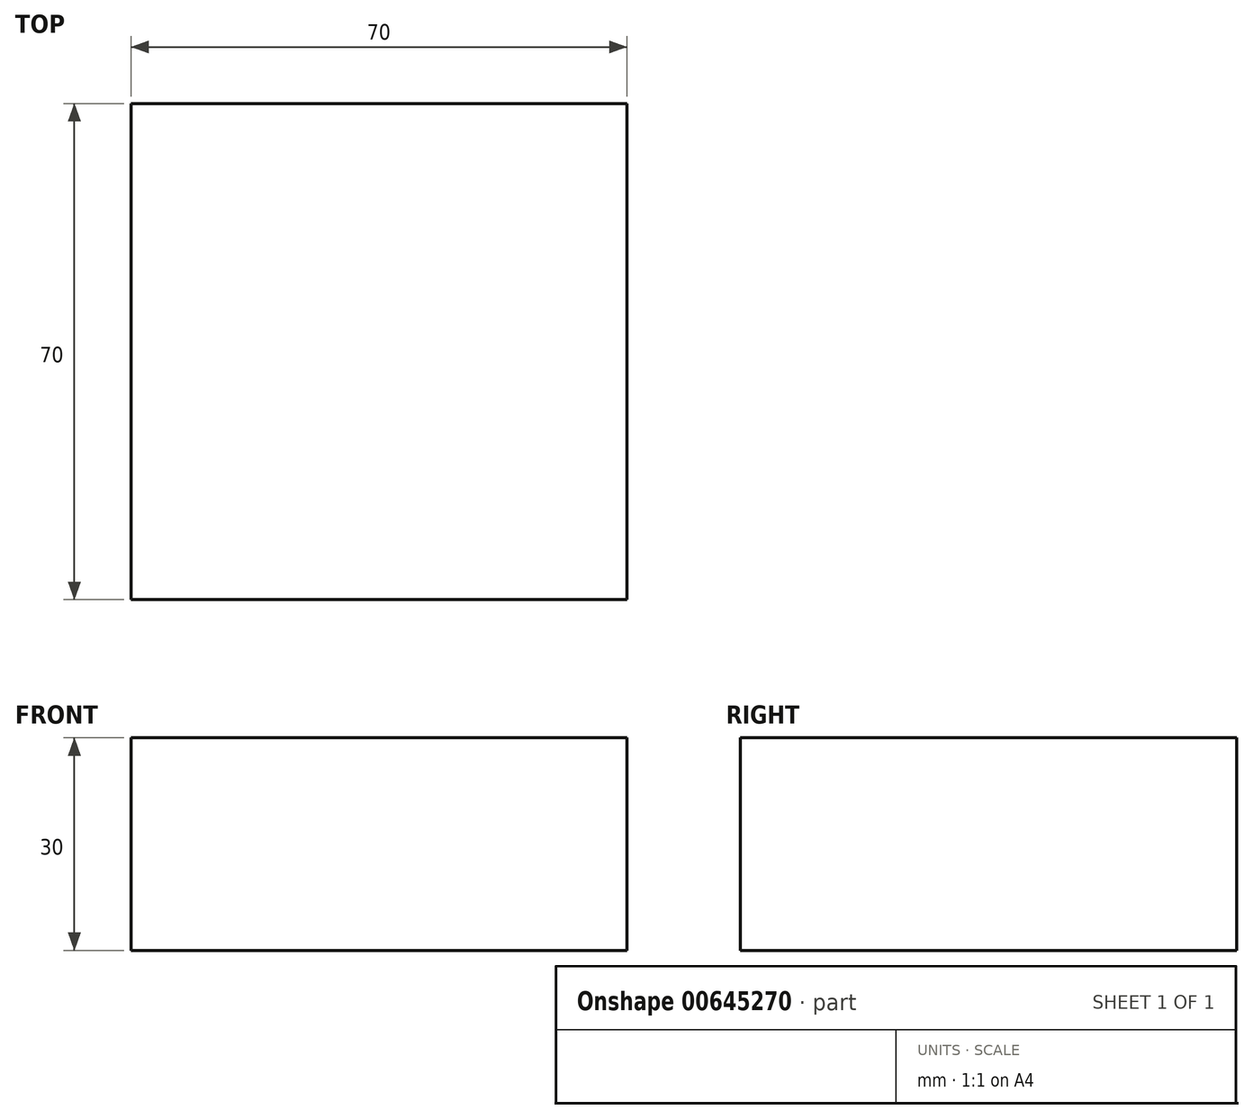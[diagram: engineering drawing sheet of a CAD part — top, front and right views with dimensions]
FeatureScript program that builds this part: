
annotation { "Feature Type Name" : "Feature", "Feature Type Description" : "" }
export const myFeature = defineFeature(function(context is Context, id is Id, definition is map)
    precondition{}
    {
        {
            var Q0;
            Q0=qCreatedBy(makeId("Top.planeOp"),FACE);
            var sketch = newSketch(context, id + "F0", { "sketchPlane" : qUnion([Q0])});
            skLineSegment(sketch, "E0.bottom", {"start": v(-37.1, 44.21) * mm, "end": v(32.9, 44.21) * mm});
            skLineSegment(sketch, "E0.top", {"start": v(-37.1, -25.79) * mm, "end": v(32.9, -25.79) * mm});
            skLineSegment(sketch, "E0.left", {"start": v(-37.1, 44.21) * mm, "end": v(-37.1, -25.79) * mm});
            skLineSegment(sketch, "E0.right", {"start": v(32.9, 44.21) * mm, "end": v(32.9, -25.79) * mm});
            skSolve(sketch);
        }
        {
            var Q0;
            Q0=makeQuery(id+"F0.imprint","IMPRINT",FACE,{"disambiguationData":[TD([[makeQuery(id+"F0.imprint","IMPRINT",EDGE,{"derivedFrom":sQuery(id+"F0.wireOp",EDGE,"E0.bottom")}),-1.0]])]});
            extrude(context, id + "F1", {"entities" : qUnion([Q0]), "depth" : 30 * mm, "offsetDistance" : 25.4 * mm});
        }
    });
